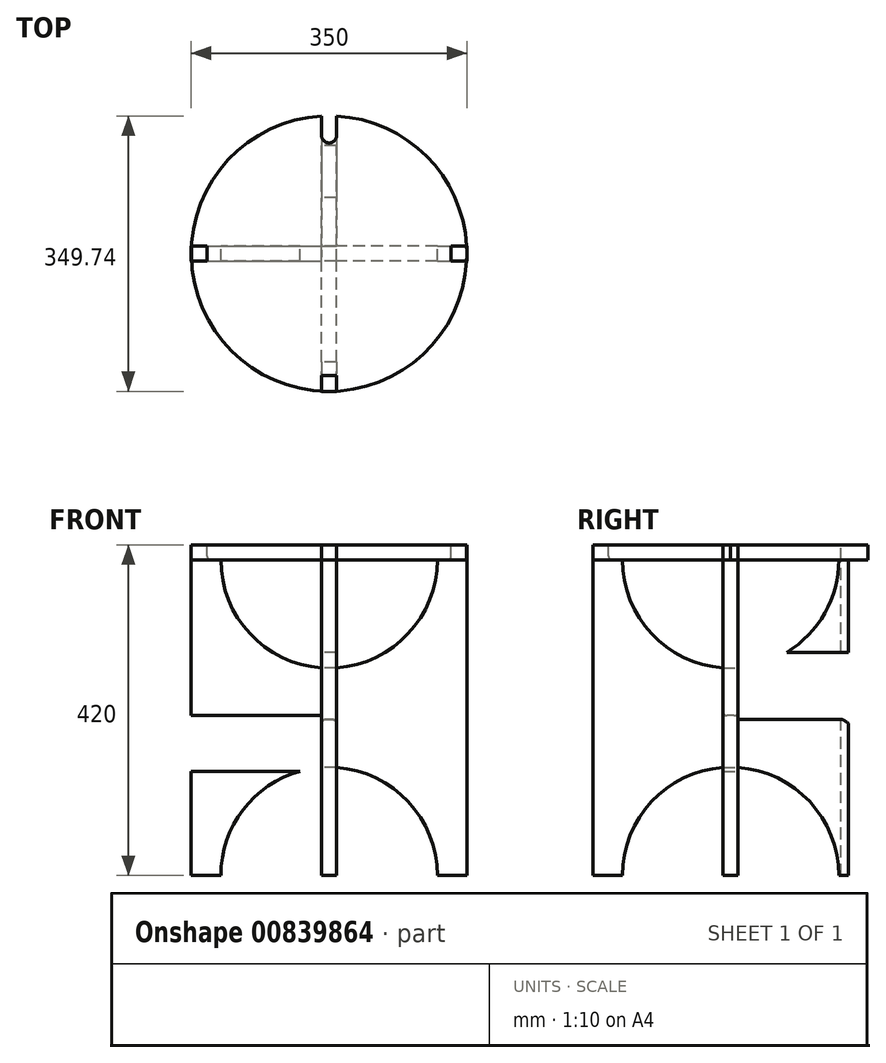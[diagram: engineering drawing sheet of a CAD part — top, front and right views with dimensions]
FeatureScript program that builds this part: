
annotation { "Feature Type Name" : "Feature", "Feature Type Description" : "" }
export const myFeature = defineFeature(function(context is Context, id is Id, definition is map)
    precondition{}
    {
        {
            var Q0;
            Q0=qCreatedBy(makeId("Front.planeOp"),FACE);
            var sketch = newSketch(context, id + "F0", { "sketchPlane" : qUnion([Q0])});
            skLineSegment(sketch, "E0.bottom", {"start": v(-175, -210) * mm, "end": v(-137.5, -210) * mm});
            skLineSegment(sketch, "E0.top", {"start": v(-175, 210) * mm, "end": v(-155, 210) * mm});
            skLineSegment(sketch, "E0.left", {"start": v(-175, -210) * mm, "end": v(-175, 210) * mm});
            skLineSegment(sketch, "E0.right", {"start": v(175, -210) * mm, "end": v(175, 210) * mm});
            skPoint(sketch, "E0.middle", {"position": v(0, 0) * mm});
            skArc(sketch, "E1", {"start": v(137.5, -210) * mm, "mid": v(0, -72.5) * mm, "end": v(-137.5, -210) * mm});
            skLineSegment(sketch, "E2.trimOffspring", {"start": v(155, 210) * mm, "end": v(175, 210) * mm});
            skLineSegment(sketch, "E3.trimOffspring", {"start": v(137.5, -210) * mm, "end": v(175, -210) * mm});
            skLineSegment(sketch, "E4.bottom", {"start": v(-155, 191) * mm, "end": v(-137.5, 191) * mm});
            skLineSegment(sketch, "E4.left", {"start": v(-155, 191) * mm, "end": v(-155, 210) * mm});
            skLineSegment(sketch, "E4.right", {"start": v(155, 191) * mm, "end": v(155, 210) * mm});
            skPoint(sketch, "E4.middle", {"position": v(0, 210) * mm});
            skPoint(sketch, "E5.orphan", {"position": v(-155, 229) * mm});
            skLineSegment(sketch, "E6.trimOffspring", {"start": v(137.5, 191) * mm, "end": v(155, 191) * mm});
            skPoint(sketch, "E7.orphan", {"position": v(155, 229) * mm});
            skLineSegment(sketch, "E8", {"start": v(-137.5, 191) * mm, "end": v(137.5, 191) * mm, "construction": true});
            skArc(sketch, "E9", {"start": v(-137.5, 191) * mm, "mid": v(0, 53.5) * mm, "end": v(137.5, 191) * mm});
            skSolve(sketch);
        }
        {
            var Q0;
            Q0 = qSketchRegion(id + "F0", true);
            extrude(context, id + "F1", {"entities" : qUnion([Q0]), "depth" : 19 / 2 * mm, "offsetDistance" : 25 * mm, "hasSecondDirection" : true, "secondDirectionOppositeDirection" : true, "secondDirectionDepth" : (19 / 2) * mm});
        }
        {
            var Q0;
            Q0=qCreatedBy(makeId("Right.planeOp"),FACE);
            var Q1;
            Q1=qCreatedBy(makeId("Front.planeOp"),FACE);
            cPlane(context, id + "F2", {"entities" : qUnion([Q0, Q1]), "cplaneType" : CPlaneType.MID_PLANE, "offset" : 25 * mm, "width" : 150 * mm, "height" : 150 * mm});
        }
        {
            var Q0;
            Q0=makeQuery(id+"F1.opExtrude","SWEPT_BODY",BODY,{"disambiguationData":[OSD([sQuery(id+"F0.wireOp",EDGE,"E0.bottom"),sQuery(id+"F0.wireOp",EDGE,"E0.top"),sQuery(id+"F0.wireOp",EDGE,"E0.left"),sQuery(id+"F0.wireOp",EDGE,"E0.right"),sQuery(id+"F0.wireOp",EDGE,"CcLeyuxu-n5A9-tvN2-8wmu-FIPjg4mwdDTK"),sQuery(id+"F0.wireOp",EDGE,"E1"),sQuery(id+"F0.wireOp",EDGE,"E2.trimOffspring"),sQuery(id+"F0.wireOp",EDGE,"E3.trimOffspring")])]});
            var Q1;
            Q1=qCreatedBy(id+"F2.planeOp",FACE);
            mirror(context, id + "F3", {"entities" : qUnion([Q0]), "mirrorPlane" : qUnion([Q1])});
        }
        {
            var Q0;
            Q0=makeQuery(id+"F1.opExtrude","SWEPT_FACE",FACE,{"disambiguationData":[OSD([sQuery(id+"F0.wireOp",EDGE,"E2.trimOffspring")])]});
            var sketch = newSketch(context, id + "F4", { "sketchPlane" : qUnion([Q0])});
            skCircle(sketch, "E10", {"center": v(0, 0) * mm, "radius": 175 * mm});
            skSolve(sketch);
        }
        {
            var Q0;
            {var subQ1=sQuery(id+"F0.wireOp",EDGE,"E2.trimOffspring");var subQ6=makeQuery(id+"F1.opExtrude","SWEPT_EDGE",EDGE,{"disambiguationData":[OSD([sQuery(id+"F0.wireOp",EDGE,"CcLeyuxu-n5A9-tvN2-8wmu-FIPjg4mwdDTK"),subQ1])]});Q0=makeQuery(id+"F4.imprint","IMPRINT",FACE,{"disambiguationData":[TD([[makeQuery(id+"F4.imprint","IMPRINT",EDGE,{"derivedFrom":subQ6}),1.0]])]});}
            var Q1;
            {var subQ1=sQuery(id+"F0.wireOp",EDGE,"E2.trimOffspring");var subQ6=makeQuery(id+"F1.opExtrude","SWEPT_EDGE",EDGE,{"disambiguationData":[OSD([subQ1,sQuery(id+"F0.wireOp",EDGE,"E4.right")])]});Q1=makeQuery(id+"F4.imprint","IMPRINT",FACE,{"disambiguationData":[TD([[makeQuery(id+"F4.imprint","IMPRINT",EDGE,{"derivedFrom":subQ6}),1.0]])]});}
            extrude(context, id + "F5", {"entities" : qUnion([Q0, Q1]), "oppositeDirection" : true, "depth" : 19 * mm, "offsetDistance" : 25 * mm});
        }
        {
            var Q0;
            Q0=makeQuery(id+"F5.opExtrude","CAP_FACE",FACE,{"disambiguationData":[OSD([sQuery(id+"F0.wireOp",EDGE,"CcLeyuxu-n5A9-tvN2-8wmu-FIPjg4mwdDTK"),sQuery(id+"F0.wireOp",EDGE,"E2.trimOffspring"),sQuery(id+"F4.wireOp",EDGE,"E10")])],"isStart":true});
            var sketch = newSketch(context, id + "F6", { "sketchPlane" : qUnion([Q0])});
            skLineSegment(sketch, "E11.top", {"start": v(9.5, 200) * mm, "end": v(-9.5, 200) * mm});
            skLineSegment(sketch, "E11.left", {"start": v(9.5, 150) * mm, "end": v(9.5, 200) * mm});
            skLineSegment(sketch, "E11.right", {"start": v(-9.5, 150) * mm, "end": v(-9.5, 200) * mm});
            skPoint(sketch, "E11.middle", {"position": v(0, 175) * mm});
            skArc(sketch, "E12", {"start": v(-9.5, 150) * mm, "mid": v(0, 140.5) * mm, "end": v(9.5, 150) * mm});
            skSolve(sketch);
        }
        {
            var Q0;
            Q0 = qSketchRegion(id + "F6", true);
            extrude(context, id + "F7", {"entities" : qUnion([Q0]), "operationType" : NewBodyOperationType.REMOVE, "endBound" : BoundingType.THROUGH_ALL, "oppositeDirection" : true, "depth" : 25 * mm, "offsetDistance" : 25 * mm});
        }
        {
            var Q0;
            Q0=makeQuery(id+"F1.opExtrude","SWEPT_EDGE",EDGE,{"disambiguationData":[OSD([sQuery(id+"F0.wireOp",EDGE,"E4.bottom"),sQuery(id+"F0.wireOp",EDGE,"E4.left")])]});
            var Q1;
            Q1=makeQuery(id+"F3.opPattern","COPY",EDGE,{"derivedFrom":makeQuery(id+"F1.opExtrude","SWEPT_EDGE",EDGE,{"disambiguationData":[OSD([sQuery(id+"F0.wireOp",EDGE,"E4.bottom"),sQuery(id+"F0.wireOp",EDGE,"E4.left")])]}),"instanceName":"1"});
            var Q2;
            Q2=makeQuery(id+"F1.opExtrude","SWEPT_EDGE",EDGE,{"disambiguationData":[OSD([sQuery(id+"F0.wireOp",EDGE,"E4.right"),sQuery(id+"F0.wireOp",EDGE,"E6.trimOffspring")])]});
            var Q3;
            Q3=makeQuery(id+"F3.opPattern","COPY",EDGE,{"derivedFrom":makeQuery(id+"F1.opExtrude","SWEPT_EDGE",EDGE,{"disambiguationData":[OSD([sQuery(id+"F0.wireOp",EDGE,"E4.right"),sQuery(id+"F0.wireOp",EDGE,"E6.trimOffspring")])]}),"instanceName":"1"});
            fillet(context, id + "F8", {"entities" : qUnion([Q0, Q1, Q2, Q3]), "radius" : 5 * mm, "tangentPropagation" : true, "allowEdgeOverflow" : false});
        }
        {
            var Q0;
            {var subQ0=sQuery(id+"F0.wireOp",EDGE,"E2.trimOffspring");var subQ1=sQuery(id+"F0.wireOp",EDGE,"E1");var subQ3=sQuery(id+"F0.wireOp",EDGE,"CcLeyuxu-n5A9-tvN2-8wmu-FIPjg4mwdDTK");var subQ5=sQuery(id+"F0.wireOp",EDGE,"E0.right");var subQ6=sQuery(id+"F0.wireOp",EDGE,"E3.trimOffspring");var subQ7=makeQuery(id+"F1.opExtrude","CAP_FACE",FACE,{"disambiguationData":[OSD([sQuery(id+"F0.wireOp",EDGE,"E0.bottom"),sQuery(id+"F0.wireOp",EDGE,"E0.top"),sQuery(id+"F0.wireOp",EDGE,"E0.left"),subQ5,subQ3,subQ1,subQ0,subQ6])],"isStart":false});Q0=makeQuery(id+"F3.boolean.opBoolean","SPLIT",FACE,{"disambiguationData":[TD([makeQuery(id+"F1.opExtrude","SWEPT_FACE",FACE,{"disambiguationData":[OSD([subQ5])]})])],"derivedFrom":subQ7});}
            var sketch = newSketch(context, id + "F9", { "sketchPlane" : qUnion([Q0])});
            skLineSegment(sketch, "E13", {"start": v(0, -72.5) * mm, "end": v(0, 53.5) * mm, "construction": true});
            skLineSegment(sketch, "E14", {"start": v(0, -9.5) * mm, "end": v(0, 53.5) * mm, "construction": true});
            skLineSegment(sketch, "E15.top", {"start": v(9.5, 53.5) * mm, "end": v(-9.5, 53.5) * mm, "construction": true});
            skLineSegment(sketch, "E15.left", {"start": v(9.5, -9.5) * mm, "end": v(9.5, 53.5) * mm});
            skLineSegment(sketch, "E15.right", {"start": v(-9.5, -9.5) * mm, "end": v(-9.5, 53.5) * mm});
            skPoint(sketch, "E15.middle", {"position": v(0, 22) * mm});
            skLineSegment(sketch, "E16.top", {"start": v(-9.5, 73.5) * mm, "end": v(9.5, 73.5) * mm});
            skLineSegment(sketch, "E16.left", {"start": v(-9.5, 53.5) * mm, "end": v(-9.5, 73.5) * mm});
            skLineSegment(sketch, "E16.right", {"start": v(9.5, 53.5) * mm, "end": v(9.5, 73.5) * mm});
            skLineSegment(sketch, "E17.bottom", {"start": v(-9.5, -9.5) * mm, "end": v(9.5, -9.5) * mm, "construction": true});
            skLineSegment(sketch, "E17.top", {"start": v(-9.5, -12) * mm, "end": v(9.5, -12) * mm});
            skLineSegment(sketch, "E17.left", {"start": v(-9.5, -9.5) * mm, "end": v(-9.5, -12) * mm});
            skLineSegment(sketch, "E17.right", {"start": v(9.5, -9.5) * mm, "end": v(9.5, -12) * mm});
            skSolve(sketch);
        }
        {
            var Q0;
            Q0 = qSketchRegion(id + "F9", true);
            extrude(context, id + "F10", {"entities" : qUnion([Q0]), "operationType" : NewBodyOperationType.REMOVE, "endBound" : BoundingType.THROUGH_ALL, "oppositeDirection" : true, "depth" : 25 * mm, "offsetDistance" : 25 * mm});
        }
        {
            var Q0;
            Q0=makeQuery(id+"F3.opPattern","COPY",FACE,{"derivedFrom":makeQuery(id+"F1.opExtrude","CAP_FACE",FACE,{"disambiguationData":[OSD([sQuery(id+"F0.wireOp",EDGE,"E0.bottom"),sQuery(id+"F0.wireOp",EDGE,"E0.top"),sQuery(id+"F0.wireOp",EDGE,"E0.left"),sQuery(id+"F0.wireOp",EDGE,"E0.right"),sQuery(id+"F0.wireOp",EDGE,"CcLeyuxu-n5A9-tvN2-8wmu-FIPjg4mwdDTK"),sQuery(id+"F0.wireOp",EDGE,"E1"),sQuery(id+"F0.wireOp",EDGE,"E2.trimOffspring"),sQuery(id+"F0.wireOp",EDGE,"E3.trimOffspring")])],"isStart":false}),"instanceName":"1"});
            var sketch = newSketch(context, id + "F11", { "sketchPlane" : qUnion([Q0])});
            skPoint(sketch, "E18.middle", {"position": v(0, 53.5) * mm});
            skLineSegment(sketch, "E19", {"start": v(0, 53.5) * mm, "end": v(0, -72.5) * mm, "construction": true});
            skLineSegment(sketch, "E20", {"start": v(0, -72.5) * mm, "end": v(0, -9.5) * mm, "construction": true});
            skLineSegment(sketch, "E21.left", {"start": v(-9.5, -72.5) * mm, "end": v(-9.5, -9.5) * mm});
            skLineSegment(sketch, "E21.right", {"start": v(9.5, -72.5) * mm, "end": v(9.5, -9.5) * mm});
            skPoint(sketch, "E21.middle", {"position": v(0, -41) * mm});
            skLineSegment(sketch, "E22.bottom", {"start": v(9.5, -9.5) * mm, "end": v(-9.5, -9.5) * mm, "construction": true});
            skLineSegment(sketch, "E22.top", {"start": v(9.5, -7) * mm, "end": v(-9.5, -7) * mm});
            skLineSegment(sketch, "E22.left", {"start": v(9.5, -9.5) * mm, "end": v(9.5, -7) * mm});
            skLineSegment(sketch, "E22.right", {"start": v(-9.5, -9.5) * mm, "end": v(-9.5, -7) * mm});
            skLineSegment(sketch, "E23.bottom", {"start": v(9.5, -72.5) * mm, "end": v(-9.5, -72.5) * mm, "construction": true});
            skLineSegment(sketch, "E23.top", {"start": v(9.5, -77.5) * mm, "end": v(-9.5, -77.5) * mm});
            skLineSegment(sketch, "E23.left", {"start": v(9.5, -72.5) * mm, "end": v(9.5, -77.5) * mm});
            skLineSegment(sketch, "E23.right", {"start": v(-9.5, -72.5) * mm, "end": v(-9.5, -77.5) * mm});
            skSolve(sketch);
        }
        {
            var Q0;
            Q0 = qSketchRegion(id + "F11", true);
            extrude(context, id + "F12", {"entities" : qUnion([Q0]), "operationType" : NewBodyOperationType.REMOVE, "endBound" : BoundingType.THROUGH_ALL, "oppositeDirection" : true, "depth" : 25 * mm, "offsetDistance" : 25 * mm});
        }
        {
            var Q0;
            Q0=makeQuery(id+"F10.boolean.opBoolean","COPY",EDGE,{"derivedFrom":makeQuery(id+"F10.opExtrude","SWEPT_EDGE",EDGE,{"disambiguationData":[OSD([sQuery(id+"F9.wireOp",EDGE,"E17.top"),sQuery(id+"F9.wireOp",EDGE,"E17.left")])]})});
            var Q1;
            Q1=makeQuery(id+"F10.boolean.opBoolean","COPY",EDGE,{"derivedFrom":makeQuery(id+"F10.opExtrude","SWEPT_EDGE",EDGE,{"disambiguationData":[OSD([sQuery(id+"F9.wireOp",EDGE,"E17.top"),sQuery(id+"F9.wireOp",EDGE,"E17.right")])]})});
            fillet(context, id + "F13", {"entities" : qUnion([Q0, Q1]), "radius" : 5 * mm, "tangentPropagation" : true, "allowEdgeOverflow" : false});
        }
        {
            var Q0;
            Q0=makeQuery(id+"F12.boolean.opBoolean","COPY",EDGE,{"derivedFrom":makeQuery(id+"F12.opExtrude","SWEPT_EDGE",EDGE,{"disambiguationData":[OSD([sQuery(id+"F11.wireOp",EDGE,"E22.top"),sQuery(id+"F11.wireOp",EDGE,"E22.right")])]})});
            var Q1;
            Q1=makeQuery(id+"F12.boolean.opBoolean","COPY",EDGE,{"derivedFrom":makeQuery(id+"F12.opExtrude","SWEPT_EDGE",EDGE,{"disambiguationData":[OSD([sQuery(id+"F11.wireOp",EDGE,"E22.top"),sQuery(id+"F11.wireOp",EDGE,"E22.left")])]})});
            fillet(context, id + "F14", {"entities" : qUnion([Q0, Q1]), "radius" : 5 * mm, "tangentPropagation" : true, "allowEdgeOverflow" : false});
        }
    });
